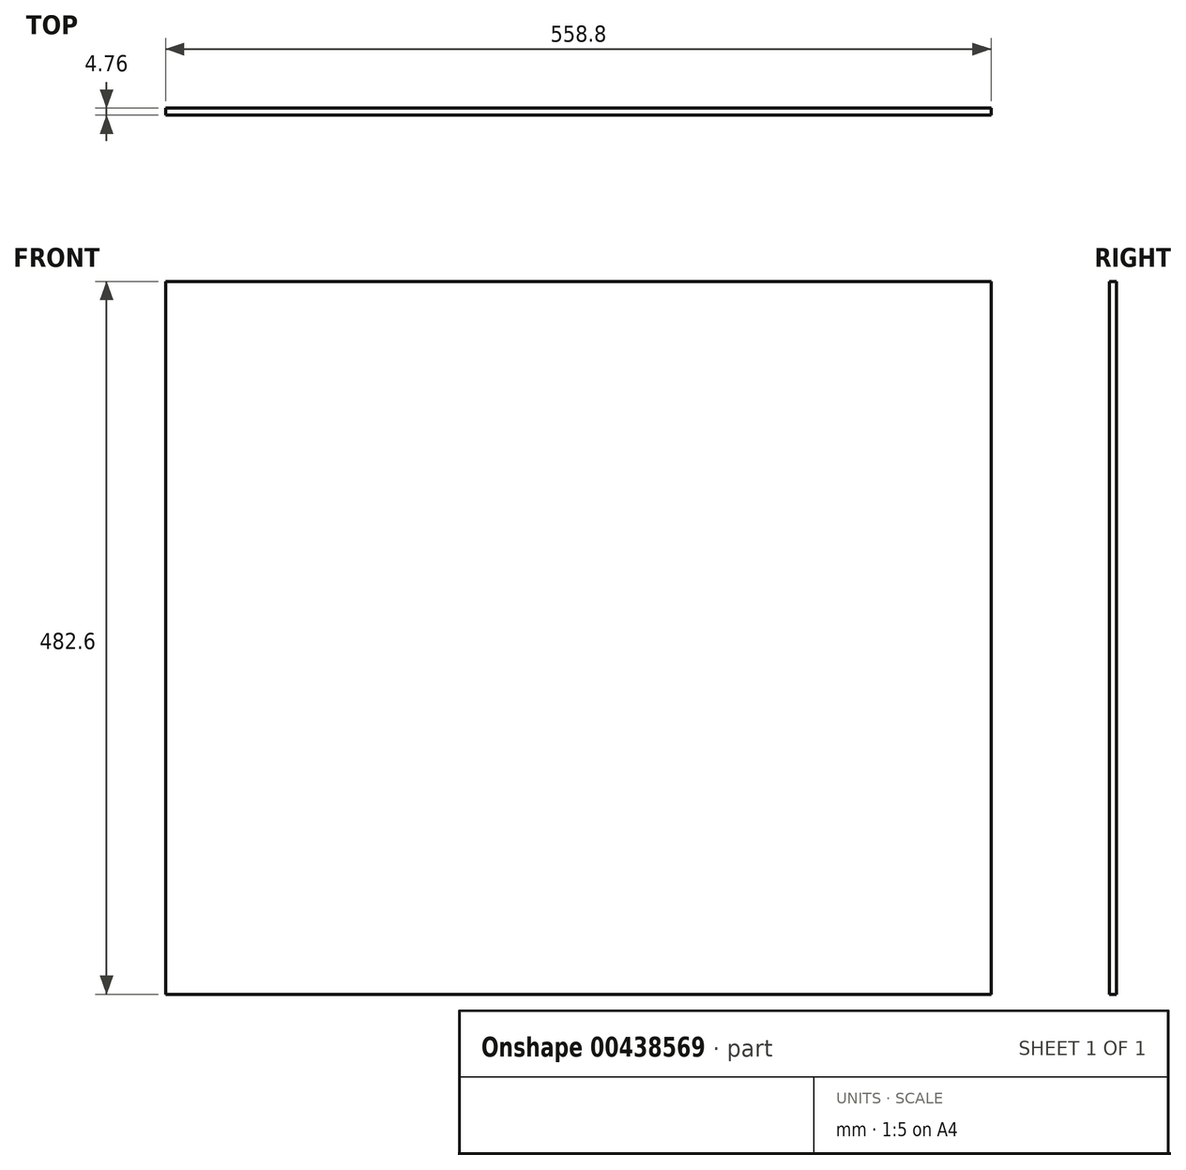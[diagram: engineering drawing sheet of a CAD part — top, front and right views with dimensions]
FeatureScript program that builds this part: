
annotation { "Feature Type Name" : "Feature", "Feature Type Description" : "" }
export const myFeature = defineFeature(function(context is Context, id is Id, definition is map)
    precondition{}
    {
        {
            var Q0;
            Q0=qCreatedBy(makeId("Front.planeOp"),FACE);
            var sketch = newSketch(context, id + "F0", { "sketchPlane" : qUnion([Q0])});
            skLineSegment(sketch, "E0.bottom", {"start": v(-281.7, 206.34) * mm, "end": v(277.1, 206.34) * mm});
            skLineSegment(sketch, "E0.top", {"start": v(-281.7, -276.26) * mm, "end": v(277.1, -276.26) * mm});
            skLineSegment(sketch, "E0.left", {"start": v(-281.7, 206.34) * mm, "end": v(-281.7, -276.26) * mm});
            skLineSegment(sketch, "E0.right", {"start": v(277.1, 206.34) * mm, "end": v(277.1, -276.26) * mm});
            skSolve(sketch);
        }
        {
            var Q0;
            Q0=makeQuery(id+"F0.imprint","IMPRINT",FACE,{"disambiguationData":[TD([[makeQuery(id+"F0.imprint","IMPRINT",EDGE,{"derivedFrom":sQuery(id+"F0.wireOp",EDGE,"E0.bottom")}),-1.0]])]});
            extrude(context, id + "F1", {"entities" : qUnion([Q0]), "depth" : 4.76 * mm});
        }
    });
